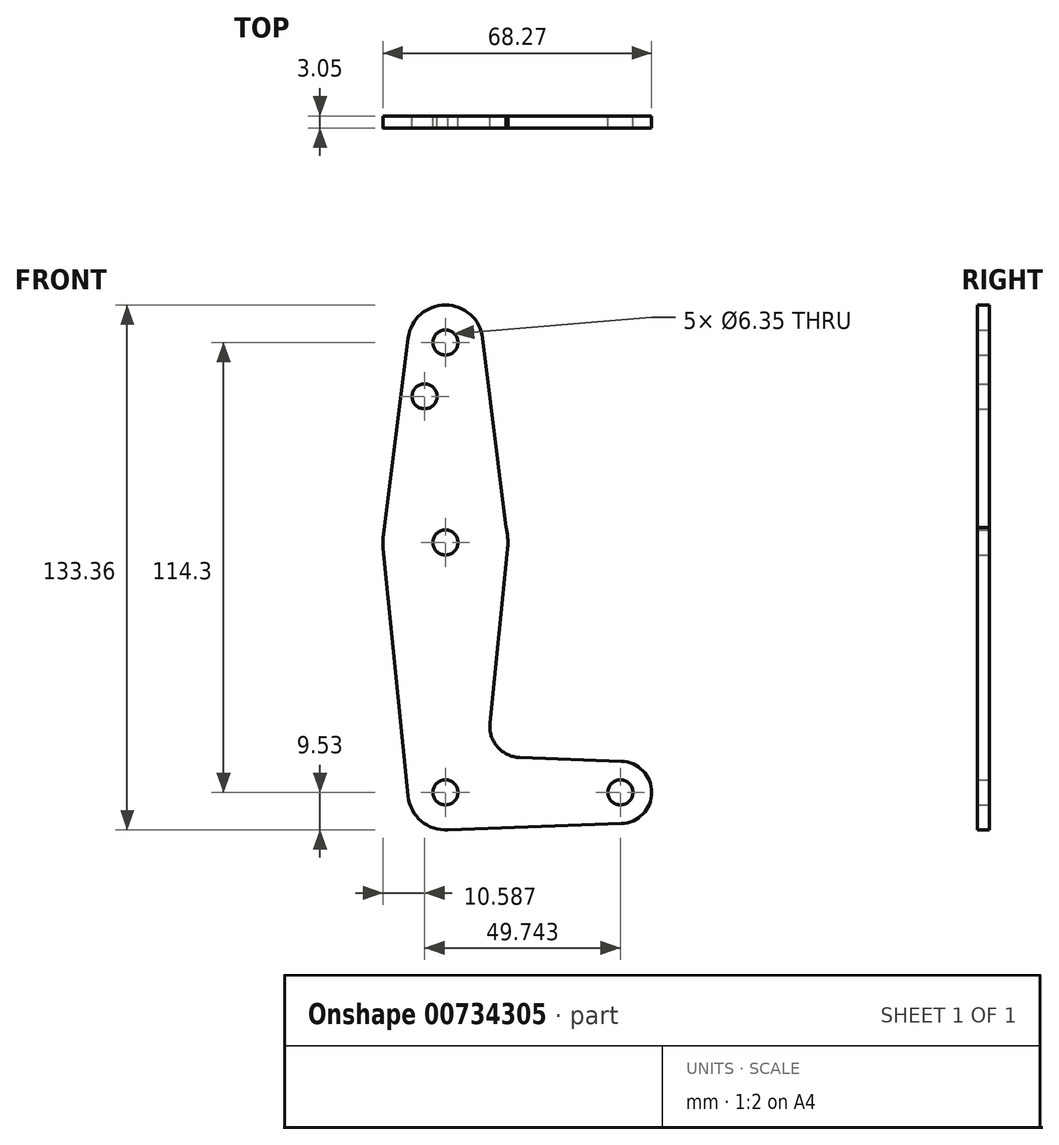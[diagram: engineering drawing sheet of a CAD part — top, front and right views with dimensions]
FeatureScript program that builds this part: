
annotation { "Feature Type Name" : "Feature", "Feature Type Description" : "" }
export const myFeature = defineFeature(function(context is Context, id is Id, definition is map)
    precondition{}
    {
        {
            var Q0;
            Q0=qCreatedBy(makeId("Front.planeOp"),FACE);
            var sketch = newSketch(context, id + "F0", { "sketchPlane" : qUnion([Q0])});
            skLineSegment(sketch, "E0", {"start": v(0, 0) * mm, "end": v(0, 114.3) * mm});
            skLineSegment(sketch, "E1", {"start": v(0, 114.3) * mm, "end": v(0, 0) * mm, "construction": true});
            skLineSegment(sketch, "E2", {"start": v(44.45, 0) * mm, "end": v(0, 0) * mm, "construction": true});
            skCircle(sketch, "E3", {"center": v(0, 114.3) * mm, "radius": 9.53 * mm});
            skCircle(sketch, "E4", {"center": v(0, 0) * mm, "radius": 9.53 * mm});
            skCircle(sketch, "E5", {"center": v(44.45, 0) * mm, "radius": 7.94 * mm});
            skCircle(sketch, "E6", {"center": v(0, 63.5) * mm, "radius": 15.88 * mm});
            skLineSegment(sketch, "E7", {"start": v(11.3, 17.6) * mm, "end": v(15.8, 61.9) * mm});
            skLineSegment(sketch, "E8", {"start": v(15.88, 63.5) * mm, "end": v(9.45, 115.47) * mm});
            skLineSegment(sketch, "E9", {"start": v(18.93, 8.85) * mm, "end": v(44.73, 7.93) * mm});
            skLineSegment(sketch, "E10", {"start": v(0, -9.53) * mm, "end": v(44.73, -7.93) * mm});
            skPoint(sketch, "E11.end.orphan", {"position": v(-9.57, 0) * mm});
            skLineSegment(sketch, "E12", {"start": v(-9.45, 115.5) * mm, "end": v(-15.75, 65.48) * mm});
            skLineSegment(sketch, "E13", {"start": v(-15.8, 61.91) * mm, "end": v(-9.48, -0.95) * mm});
            skCircle(sketch, "E14", {"center": v(0, 63.5) * mm, "radius": 3.18 * mm});
            skCircle(sketch, "E15", {"center": v(0, 114.3) * mm, "radius": 3.18 * mm});
            skCircle(sketch, "E16", {"center": v(0, 0) * mm, "radius": 3.18 * mm});
            skCircle(sketch, "E17", {"center": v(44.45, 0) * mm, "radius": 3.18 * mm});
            skPoint(sketch, "E18", {"position": v(-5.3, 100.63) * mm});
            skCircle(sketch, "E19", {"center": v(-5.3, 100.63) * mm, "radius": 3.18 * mm});
            skArc(sketch, "E20.filletArc", {"start": v(11.3, 17.6) * mm, "mid": v(13.22, 11.57) * mm, "end": v(18.93, 8.85) * mm});
            skSolve(sketch);
        }
        {
            var Q0;
            Q0 = qSketchRegion(id + "F0", true);
            extrude(context, id + "F1", {"entities" : qUnion([Q0]), "depth" : 3.05 * mm, "offsetDistance" : 25.4 * mm});
        }
    });
